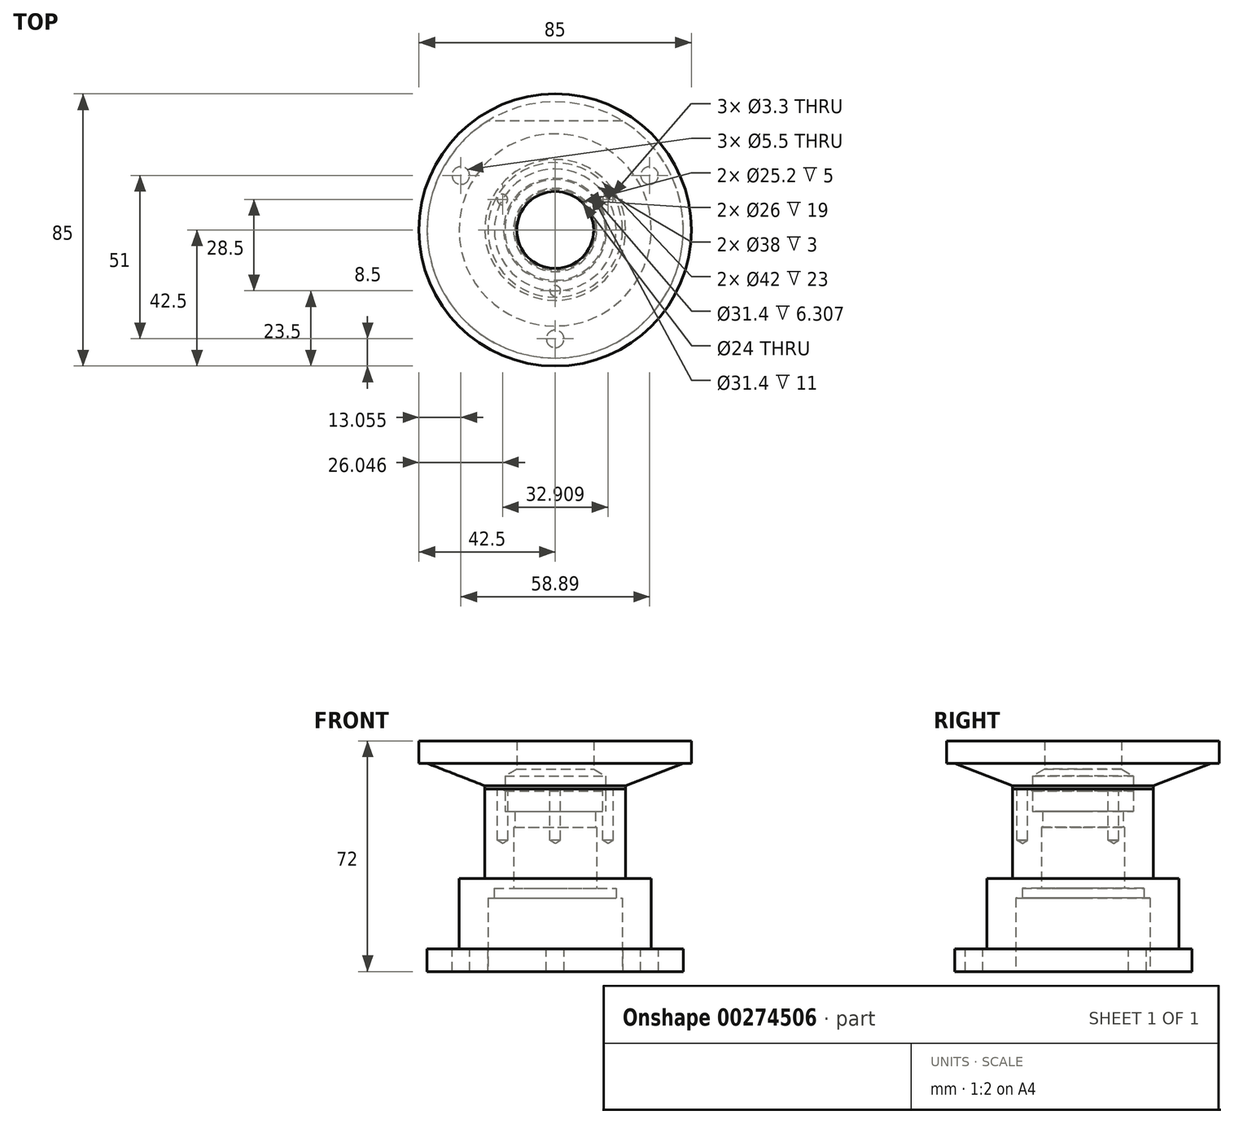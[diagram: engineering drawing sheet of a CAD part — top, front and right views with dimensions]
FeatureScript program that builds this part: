
annotation { "Feature Type Name" : "Feature", "Feature Type Description" : "" }
export const myFeature = defineFeature(function(context is Context, id is Id, definition is map)
    precondition{}
    {
        {
            var Q0;
            Q0=qCreatedBy(makeId("Front.planeOp"),FACE);
            var sketch = newSketch(context, id + "F0", { "sketchPlane" : qUnion([Q0])});
            skLineSegment(sketch, "E0.bottom", {"start": v(42.5, 72) * mm, "end": v(0, 72) * mm});
            skLineSegment(sketch, "E0.top", {"start": v(42.5, -1) * mm, "end": v(0, -1) * mm});
            skLineSegment(sketch, "E0.left", {"start": v(42.5, 72) * mm, "end": v(42.5, -1) * mm});
            skPoint(sketch, "E0.middle", {"position": v(0, 0) * mm});
            skLineSegment(sketch, "E1", {"start": v(0, 0) * mm, "end": v(0, 72) * mm, "construction": true});
            skLineSegment(sketch, "E2", {"start": v(0, 72) * mm, "end": v(0, -1) * mm});
            skPoint(sketch, "E0.right.end.orphan", {"position": v(-42.5, -1) * mm});
            skPoint(sketch, "E3.orphan", {"position": v(-42.5, 72) * mm});
            skSolve(sketch);
        }
        {
            var Q0;
            Q0=qCreatedBy(makeId("Front.planeOp"),FACE);
            var sketch = newSketch(context, id + "F1", { "sketchPlane" : qUnion([Q0])});
            skLineSegment(sketch, "E4", {"start": v(0, -43.75) * mm, "end": v(0, 56.25) * mm, "construction": true});
            skLineSegment(sketch, "E5", {"start": v(21, 0) * mm, "end": v(40, 0) * mm});
            skLineSegment(sketch, "E6", {"start": v(40, 0) * mm, "end": v(40, 7) * mm});
            skLineSegment(sketch, "E7", {"start": v(40, 7) * mm, "end": v(30, 7) * mm});
            skLineSegment(sketch, "E8", {"start": v(30, 7) * mm, "end": v(30, 29) * mm});
            skLineSegment(sketch, "E9", {"start": v(30, 29) * mm, "end": v(22, 29) * mm});
            skLineSegment(sketch, "E10", {"start": v(22, 29) * mm, "end": v(22, 57) * mm});
            skLineSegment(sketch, "E11", {"start": v(22, 57) * mm, "end": v(16.1, 57) * mm});
            skLineSegment(sketch, "E12", {"start": v(15.7, 56.3) * mm, "end": v(15.7, 50) * mm});
            skLineSegment(sketch, "E13", {"start": v(15.7, 50) * mm, "end": v(12.6, 50) * mm});
            skLineSegment(sketch, "E14", {"start": v(12.6, 50) * mm, "end": v(12.6, 45) * mm});
            skLineSegment(sketch, "E15", {"start": v(12.6, 45) * mm, "end": v(13, 45) * mm});
            skLineSegment(sketch, "E16", {"start": v(13, 45) * mm, "end": v(13, 26) * mm});
            skLineSegment(sketch, "E17", {"start": v(13, 26) * mm, "end": v(19, 26) * mm});
            skLineSegment(sketch, "E18", {"start": v(19, 26) * mm, "end": v(19, 23) * mm});
            skLineSegment(sketch, "E19", {"start": v(19, 23) * mm, "end": v(21, 23) * mm});
            skLineSegment(sketch, "E20", {"start": v(21, 23) * mm, "end": v(21, 0) * mm});
            skLineSegment(sketch, "E21.MirrorCS", {"start": v(-19, 26) * mm, "end": v(-19, 23) * mm, "construction": true});
            skLineSegment(sketch, "E22.MirrorCS", {"start": v(-12.6, 45) * mm, "end": v(-13, 45) * mm, "construction": true});
            skLineSegment(sketch, "E23.MirrorCS", {"start": v(-21, 0) * mm, "end": v(-40, 0) * mm, "construction": true});
            skLineSegment(sketch, "E24.MirrorCS", {"start": v(-40, 0) * mm, "end": v(-40, 7) * mm, "construction": true});
            skLineSegment(sketch, "E25.MirrorCS", {"start": v(-19, 23) * mm, "end": v(-21, 23) * mm, "construction": true});
            skLineSegment(sketch, "E26.MirrorCS", {"start": v(-40, 7) * mm, "end": v(-30, 7) * mm, "construction": true});
            skLineSegment(sketch, "E27.MirrorCS", {"start": v(-21, 23) * mm, "end": v(-21, 0) * mm, "construction": true});
            skLineSegment(sketch, "E28.MirrorCS", {"start": v(-30, 7) * mm, "end": v(-30, 29) * mm, "construction": true});
            skLineSegment(sketch, "E29.MirrorCS", {"start": v(-13, 26) * mm, "end": v(-19, 26) * mm, "construction": true});
            skLineSegment(sketch, "E30.MirrorCS", {"start": v(-30, 29) * mm, "end": v(-22, 29) * mm, "construction": true});
            skLineSegment(sketch, "E31.MirrorCS", {"start": v(-15.7, 56.3) * mm, "end": v(-15.7, 50) * mm, "construction": true});
            skLineSegment(sketch, "E32.MirrorCS", {"start": v(-15.7, 50) * mm, "end": v(-12.6, 50) * mm, "construction": true});
            skLineSegment(sketch, "E33.MirrorCS", {"start": v(-12.6, 50) * mm, "end": v(-12.6, 45) * mm, "construction": true});
            skLineSegment(sketch, "E34.MirrorCS", {"start": v(-13, 45) * mm, "end": v(-13, 26) * mm, "construction": true});
            skLineSegment(sketch, "E35.MirrorCS", {"start": v(-22, 57) * mm, "end": v(-16.1, 57) * mm, "construction": true});
            skLineSegment(sketch, "E36.MirrorCS", {"start": v(-22, 29) * mm, "end": v(-22, 57) * mm, "construction": true});
            skPoint(sketch, "E37", {"position": v(16.1, 57) * mm});
            skPoint(sketch, "E38.MirrorP", {"position": v(-16.1, 57) * mm});
            skLineSegment(sketch, "E39", {"start": v(16.1, 57) * mm, "end": v(15.7, 56.3) * mm});
            skPoint(sketch, "E40.orphan", {"position": v(15.7, 57) * mm});
            skLineSegment(sketch, "E41.MirrorCS", {"start": v(-16.1, 57) * mm, "end": v(-15.7, 56.3) * mm, "construction": true});
            skPoint(sketch, "E42.orphan", {"position": v(-15.7, 57) * mm});
            skSolve(sketch);
        }
        {
            var Q0;
            Q0=qCreatedBy(makeId("Front.planeOp"),FACE);
            var sketch = newSketch(context, id + "F2", { "sketchPlane" : qUnion([Q0])});
            skPoint(sketch, "E43", {"position": v(22, 58) * mm});
            skLineSegment(sketch, "E44", {"start": v(40, 65) * mm, "end": v(22, 58) * mm});
            skPoint(sketch, "E45", {"position": v(30, 29) * mm});
            skPoint(sketch, "E46", {"position": v(22, 29) * mm});
            skLineSegment(sketch, "E47", {"start": v(22, 58) * mm, "end": v(22, 29) * mm});
            skLineSegment(sketch, "E48", {"start": v(30, 29) * mm, "end": v(30, 7) * mm});
            skLineSegment(sketch, "E49", {"start": v(30, 7) * mm, "end": v(40, 7) * mm});
            skLineSegment(sketch, "E50", {"start": v(40, 7) * mm, "end": v(40, 0) * mm});
            skLineSegment(sketch, "E51", {"start": v(40, 0) * mm, "end": v(21, 0) * mm});
            skLineSegment(sketch, "E52", {"start": v(21, 0) * mm, "end": v(21, 23) * mm});
            skLineSegment(sketch, "E53", {"start": v(21, 23) * mm, "end": v(19, 23) * mm});
            skLineSegment(sketch, "E54", {"start": v(19, 23) * mm, "end": v(19, 26) * mm});
            skLineSegment(sketch, "E55", {"start": v(19, 26) * mm, "end": v(13, 26) * mm});
            skLineSegment(sketch, "E56", {"start": v(13, 26) * mm, "end": v(13, 45) * mm});
            skLineSegment(sketch, "E57", {"start": v(13, 45) * mm, "end": v(12.6, 45) * mm});
            skLineSegment(sketch, "E58", {"start": v(12.6, 45) * mm, "end": v(12.6, 50) * mm});
            skLineSegment(sketch, "E59", {"start": v(12.6, 50) * mm, "end": v(15.7, 50) * mm});
            skLineSegment(sketch, "E60", {"start": v(15.7, 50) * mm, "end": v(15.7, 61) * mm});
            skLineSegment(sketch, "E61", {"start": v(12, 63.14) * mm, "end": v(12, 72) * mm});
            skLineSegment(sketch, "E62", {"start": v(40, 65) * mm, "end": v(42.5, 65) * mm});
            skLineSegment(sketch, "E63", {"start": v(42.5, 65) * mm, "end": v(42.5, 72) * mm});
            skLineSegment(sketch, "E64", {"start": v(42.5, 72) * mm, "end": v(12, 72) * mm});
            skLineSegment(sketch, "E65", {"start": v(22, 29) * mm, "end": v(30, 29) * mm});
            skLineSegment(sketch, "E66", {"start": v(15.7, 61) * mm, "end": v(12, 63.14) * mm});
            skSolve(sketch);
        }
        {
            var Q0;
            Q0 = qSketchRegion(id + "F2", true);
            var Q1;
            Q1=sQuery(id+"F1.wireOp",EDGE,"E4");
            revolve(context, id + "F3", {"surfaceOperationType" : NewSurfaceOperationType.NEW, "entities" : qUnion([Q0]), "axis" : qUnion([Q1]), "revolveType" : RevolveType.FULL});
        }
        {
            var Q0;
            Q0=makeQuery(id+"F1.imprint","IMPRINT",FACE,{"disambiguationData":[TD([[makeQuery(id+"F1.imprint","IMPRINT",EDGE,{"derivedFrom":sQuery(id+"F1.wireOp",EDGE,"E5")}),1.0]])]});
            var Q1;
            Q1=sQuery(id+"F1.wireOp",EDGE,"E4");
            revolve(context, id + "F4", {"entities" : qUnion([Q0]), "axis" : qUnion([Q1]), "revolveType" : RevolveType.FULL});
        }
        {
            var Q0;
            Q0=qCreatedBy(makeId("Front.planeOp"),FACE);
            cPlane(context, id + "F5", {"entities" : qUnion([Q0]), "cplaneType" : CPlaneType.OFFSET, "offset" : 34 * mm, "oppositeDirection" : true, "width" : 150 * mm, "height" : 150 * mm});
        }
        {
            var Q0;
            Q0=qCreatedBy(id+"F5.planeOp",FACE);
            var sketch = newSketch(context, id + "F6", { "sketchPlane" : qUnion([Q0])});
            skLineSegment(sketch, "E67.bottom", {"start": v(-40, -0.5) * mm, "end": v(40, -0.5) * mm});
            skLineSegment(sketch, "E67.top", {"start": v(-40, 7.5) * mm, "end": v(40, 7.5) * mm});
            skLineSegment(sketch, "E67.left", {"start": v(-40, -0.5) * mm, "end": v(-40, 7.5) * mm});
            skLineSegment(sketch, "E67.right", {"start": v(40, -0.5) * mm, "end": v(40, 7.5) * mm});
            skSolve(sketch);
        }
        {
            var Q0;
            Q0=makeQuery(id+"F6.imprint","IMPRINT",FACE,{"disambiguationData":[TD([[makeQuery(id+"F6.imprint","IMPRINT",EDGE,{"derivedFrom":sQuery(id+"F6.wireOp",EDGE,"E67.bottom")}),1.0]])]});
            extrude(context, id + "F7", {"entities" : qUnion([Q0]), "operationType" : NewBodyOperationType.REMOVE, "oppositeDirection" : true, "depth" : 10 * mm});
        }
        {
            var Q0;
            Q0=makeQuery(id+"F4.opRevolve","SWEPT_FACE",FACE,{"disambiguationData":[OSD([sQuery(id+"F1.wireOp",EDGE,"E11")])]});
            var sketch = newSketch(context, id + "F8", { "sketchPlane" : qUnion([Q0])});
            skPoint(sketch, "E68.center", {"position": v(0, 0) * mm});
            skCircle(sketch, "E69", {"center": v(0, 0) * mm, "radius": 19 * mm, "construction": true});
            skLineSegment(sketch, "E70", {"start": v(0, 0) * mm, "end": v(0, -19) * mm, "construction": true});
            skLineSegment(sketch, "E71.1.0", {"start": v(0, 0) * mm, "end": v(16.45, 9.5) * mm, "construction": true});
            skLineSegment(sketch, "E71.2.0", {"start": v(0, 0) * mm, "end": v(-16.45, 9.5) * mm, "construction": true});
            skPoint(sketch, "E72", {"position": v(-16.45, 9.5) * mm});
            skPoint(sketch, "E73", {"position": v(16.45, 9.5) * mm});
            skPoint(sketch, "E74", {"position": v(0, -19) * mm});
            skSolve(sketch);
        }
        {
            var Q0;
            Q0=sQuery(id+"F8.wireOp",VERTEX,"E73");
            var Q1;
            Q1=sQuery(id+"F8.wireOp",VERTEX,"E74");
            var Q2;
            Q2=sQuery(id+"F8.wireOp",VERTEX,"E72");
            var Q3;
            Q3=makeQuery(id+"F4.opRevolve","SWEPT_BODY",BODY,{"disambiguationData":[OSD([sQuery(id+"F1.wireOp",EDGE,"E5"),sQuery(id+"F1.wireOp",EDGE,"E6"),sQuery(id+"F1.wireOp",EDGE,"E7"),sQuery(id+"F1.wireOp",EDGE,"E8"),sQuery(id+"F1.wireOp",EDGE,"E9"),sQuery(id+"F1.wireOp",EDGE,"E10"),sQuery(id+"F1.wireOp",EDGE,"E11"),sQuery(id+"F1.wireOp",EDGE,"E12"),sQuery(id+"F1.wireOp",EDGE,"E13"),sQuery(id+"F1.wireOp",EDGE,"E14"),sQuery(id+"F1.wireOp",EDGE,"E15"),sQuery(id+"F1.wireOp",EDGE,"E16"),sQuery(id+"F1.wireOp",EDGE,"E17"),sQuery(id+"F1.wireOp",EDGE,"E18"),sQuery(id+"F1.wireOp",EDGE,"E19"),sQuery(id+"F1.wireOp",EDGE,"E20"),sQuery(id+"F1.wireOp",EDGE,"E39")])]});
            hole(context, id + "F9", {"style" : HoleStyle.SIMPLE, "endStyle" : HoleEndStyle.BLIND, "holeDiameter" : 3.3 * mm, "holeDepth" : 16 * mm, "tappedDepth" : 7 * mm, "tapClearance" : 3, "startFromSketch" : true, "locations" : qUnion([Q0, Q1, Q2]), "scope" : qUnion([Q3])});
        }
        {
            var Q0;
            Q0=makeQuery(id+"F4.opRevolve","SWEPT_FACE",FACE,{"disambiguationData":[OSD([sQuery(id+"F1.wireOp",EDGE,"E7")])]});
            var sketch = newSketch(context, id + "F10", { "sketchPlane" : qUnion([Q0])});
            skCircle(sketch, "E75", {"center": v(0, 0) * mm, "radius": 34 * mm, "construction": true});
            skLineSegment(sketch, "E76", {"start": v(0, 0) * mm, "end": v(0, -34) * mm, "construction": true});
            skLineSegment(sketch, "E77.1.0", {"start": v(0, 0) * mm, "end": v(29.44, 17) * mm, "construction": true});
            skLineSegment(sketch, "E77.2.0", {"start": v(0, 0) * mm, "end": v(-29.44, 17) * mm, "construction": true});
            skSolve(sketch);
        }
        {
            var Q0;
            Q0=sQuery(id+"F10.wireOp",VERTEX,"E77.2.0.end");
            var Q1;
            Q1=sQuery(id+"F10.wireOp",VERTEX,"E77.1.0.end");
            var Q2;
            Q2=sQuery(id+"F10.wireOp",VERTEX,"E76.end");
            var Q3;
            Q3=makeQuery(id+"F4.opRevolve","SWEPT_BODY",BODY,{"disambiguationData":[OSD([sQuery(id+"F1.wireOp",EDGE,"E5"),sQuery(id+"F1.wireOp",EDGE,"E6"),sQuery(id+"F1.wireOp",EDGE,"E7"),sQuery(id+"F1.wireOp",EDGE,"E8"),sQuery(id+"F1.wireOp",EDGE,"E9"),sQuery(id+"F1.wireOp",EDGE,"E10"),sQuery(id+"F1.wireOp",EDGE,"E11"),sQuery(id+"F1.wireOp",EDGE,"E12"),sQuery(id+"F1.wireOp",EDGE,"E13"),sQuery(id+"F1.wireOp",EDGE,"E14"),sQuery(id+"F1.wireOp",EDGE,"E15"),sQuery(id+"F1.wireOp",EDGE,"E16"),sQuery(id+"F1.wireOp",EDGE,"E17"),sQuery(id+"F1.wireOp",EDGE,"E18"),sQuery(id+"F1.wireOp",EDGE,"E19"),sQuery(id+"F1.wireOp",EDGE,"E20"),sQuery(id+"F1.wireOp",EDGE,"E39")])]});
            hole(context, id + "F11", {"style" : HoleStyle.SIMPLE, "endStyle" : HoleEndStyle.THROUGH, "holeDiameter" : 5.5 * mm, "tappedDepth" : 7 * mm, "tapClearance" : 3, "startFromSketch" : true, "locations" : qUnion([Q0, Q1, Q2]), "scope" : qUnion([Q3])});
        }
    });
